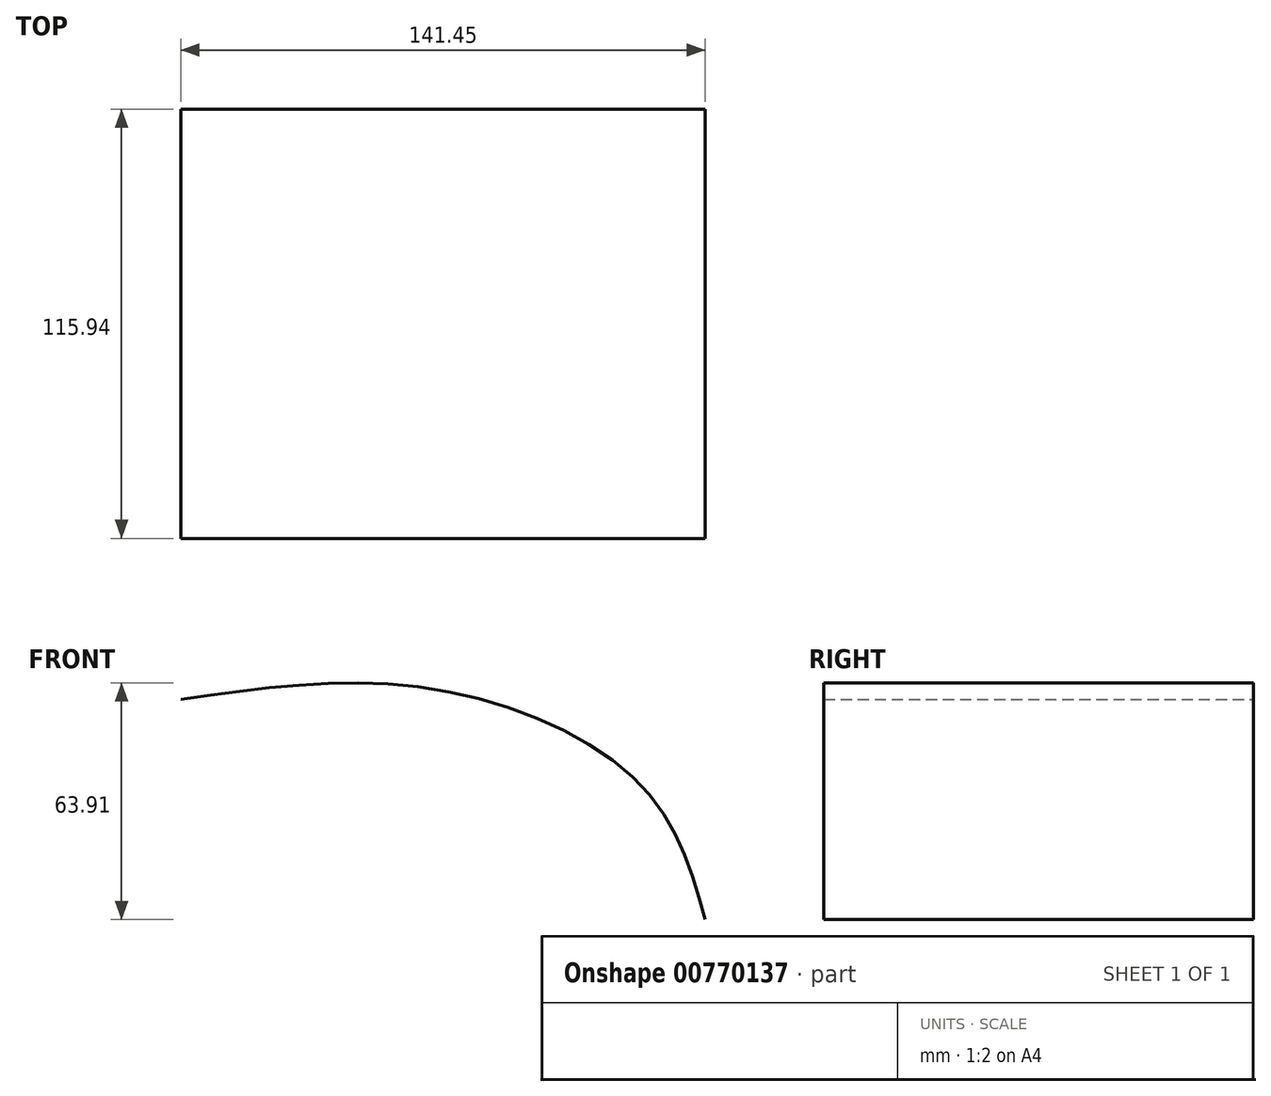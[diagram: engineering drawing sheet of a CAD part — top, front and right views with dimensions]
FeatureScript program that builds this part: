
annotation { "Feature Type Name" : "Feature", "Feature Type Description" : "" }
export const myFeature = defineFeature(function(context is Context, id is Id, definition is map)
    precondition{}
    {
        {
            var Q0;
            Q0=qCreatedBy(makeId("Front.planeOp"),FACE);
            var sketch = newSketch(context, id + "F0", { "sketchPlane" : qUnion([Q0])});
            skFitSpline(sketch, "E0", {"points": [v(-26.93, 34.57) * mm, v(40.4, 37.5) * mm, v(97.57, 11.07) * mm, v(114.52, -24.86) * mm], "startDerivative": vector(182.53, 26.59) * mm, "endDerivative": vector(37.6, -135.76) * mm});
            skSolve(sketch);
        }
        {
            var Q0;
            Q0 = qSketchRegion(id + "FyGbSAux9eksFur_0", true);
            var Q1;
            Q1=sQuery(id+"F0.wireOp",EDGE,"E0");
            extrude(context, id + "F1", {"entities" : qUnion([Q0]), "bodyType" : ToolBodyType.SURFACE, "surfaceEntities" : qUnion([Q1]), "endBound" : BoundingType.SYMMETRIC, "oppositeDirection" : true, "depth" : 115.94 * mm, "offsetDistance" : 25.4 * mm});
        }
    });
